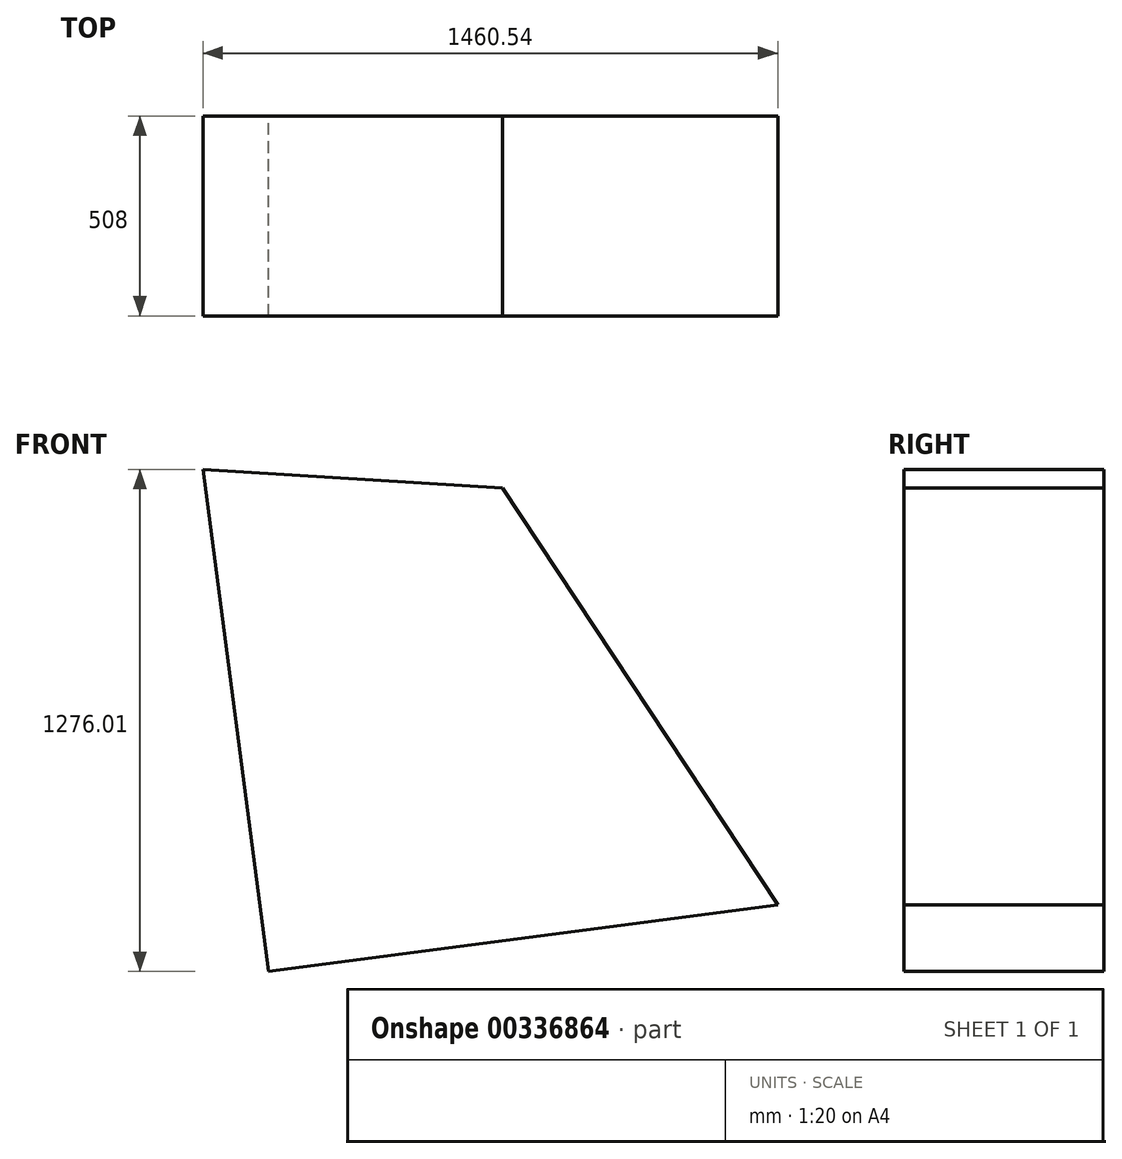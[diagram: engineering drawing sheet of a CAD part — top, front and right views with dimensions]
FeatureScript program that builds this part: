
annotation { "Feature Type Name" : "Feature", "Feature Type Description" : "" }
export const myFeature = defineFeature(function(context is Context, id is Id, definition is map)
    precondition{}
    {
        {
            var Q0;
            Q0=qCreatedBy(makeId("Front.planeOp"),FACE);
            var sketch = newSketch(context, id + "F0", { "sketchPlane" : qUnion([Q0])});
            skLineSegment(sketch, "E0", {"start": v(-724.24, 674.27) * mm, "end": v(-557.42, -601.74) * mm});
            skLineSegment(sketch, "E1", {"start": v(-557.42, -601.74) * mm, "end": v(736.3, -432.6) * mm});
            skLineSegment(sketch, "E2", {"start": v(736.3, -432.6) * mm, "end": v(36.3, 627.06) * mm});
            skLineSegment(sketch, "E3", {"start": v(36.3, 627.06) * mm, "end": v(-724.24, 674.27) * mm});
            skSolve(sketch);
        }
        {
            var Q0;
            Q0=makeQuery(id+"F0.imprint","IMPRINT",FACE,{"disambiguationData":[TD([[makeQuery(id+"F0.imprint","IMPRINT",EDGE,{"derivedFrom":sQuery(id+"F0.wireOp",EDGE,"E0")}),1.0]])]});
            extrude(context, id + "F1", {"entities" : qUnion([Q0]), "depth" : 508 * mm});
        }
    });
